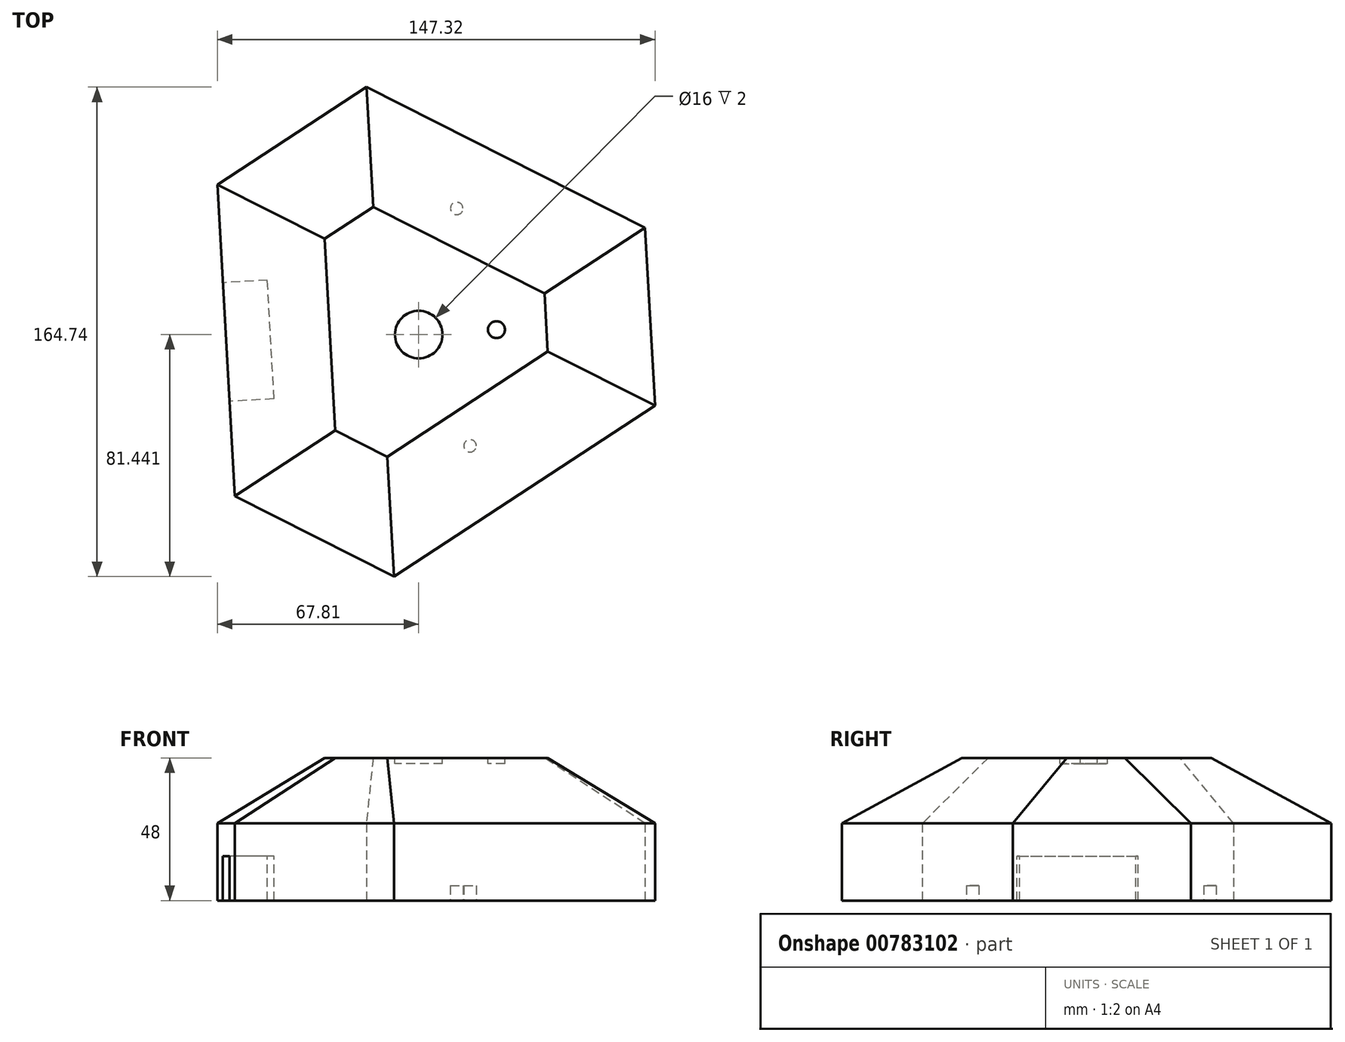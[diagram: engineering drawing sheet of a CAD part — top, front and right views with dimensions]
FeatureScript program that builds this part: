
annotation { "Feature Type Name" : "Feature", "Feature Type Description" : "" }
export const myFeature = defineFeature(function(context is Context, id is Id, definition is map)
    precondition{}
    {
        {
            var Q0;
            Q0=qCreatedBy(makeId("Top.planeOp"),FACE);
            var sketch = newSketch(context, id + "F0", { "sketchPlane" : qUnion([Q0])});
            skCircle(sketch, "E0.cCircle", {"center": v(0, 0) * mm, "radius": 64.95 * mm, "construction": true});
            skLineSegment(sketch, "E0.0", {"start": v(129.7, 7.33) * mm, "end": v(-58.5, -115.99) * mm});
            skLineSegment(sketch, "E0.1", {"start": v(-58.5, -115.99) * mm, "end": v(-71.2, 108.66) * mm});
            skLineSegment(sketch, "E0.2", {"start": v(-71.2, 108.66) * mm, "end": v(129.7, 7.33) * mm});
            skPoint(sketch, "E0.0.midPoint", {"position": v(35.6, -54.33) * mm});
            skPoint(sketch, "E1", {"position": v(-17.63, 81.64) * mm});
            skPoint(sketch, "E2", {"position": v(-67.81, 48.75) * mm});
            skPoint(sketch, "E3", {"position": v(-61.9, -55.99) * mm});
            skPoint(sketch, "E4", {"position": v(-8.31, -83.1) * mm});
            skPoint(sketch, "E5", {"position": v(79.51, -25.55) * mm});
            skPoint(sketch, "E6", {"position": v(76.13, 34.35) * mm});
            skLineSegment(sketch, "E7", {"start": v(-61.9, -55.99) * mm, "end": v(-8.31, -83.1) * mm});
            skLineSegment(sketch, "E8", {"start": v(79.51, -25.55) * mm, "end": v(76.13, 34.35) * mm});
            skLineSegment(sketch, "E9", {"start": v(-17.63, 81.64) * mm, "end": v(-67.81, 48.75) * mm});
            skSolve(sketch);
        }
        {
            var Q0;
            {var subQ3=sQuery(id+"F0.wireOp",EDGE,"E7");Q0=makeQuery(id+"F0.imprint","IMPRINT",FACE,{"disambiguationData":[TD([[makeQuery(id+"F0.imprint","IMPRINT",EDGE,{"derivedFrom":subQ3}),1.0]])]});}
            extrude(context, id + "F1", {"entities" : qUnion([Q0]), "depth" : 48 * mm, "offsetDistance" : 25 * mm});
        }
        {
            var Q0;
            Q0=makeQuery(id+"F1.opExtrude","CAP_FACE",FACE,{"disambiguationData":[OSD([sQuery(id+"F0.wireOp",EDGE,"E0.0"),sQuery(id+"F0.wireOp",EDGE,"E0.1"),sQuery(id+"F0.wireOp",EDGE,"E0.2"),sQuery(id+"F0.wireOp",EDGE,"E7"),sQuery(id+"F0.wireOp",EDGE,"E8"),sQuery(id+"F0.wireOp",EDGE,"E9")])],"isStart":false});
            chamfer(context, id + "F2", {"entities" : qUnion([Q0]), "chamferType" : ChamferType.TWO_OFFSETS, "width1" : 22 * mm, "oppositeDirection" : false, "width2" : 35 * mm, "tangentPropagation" : true});
        }
        {
            var Q0;
            Q0=makeQuery(id+"F1.opExtrude","CAP_FACE",FACE,{"disambiguationData":[OSD([sQuery(id+"F0.wireOp",EDGE,"E0.0"),sQuery(id+"F0.wireOp",EDGE,"E0.1"),sQuery(id+"F0.wireOp",EDGE,"E0.2"),sQuery(id+"F0.wireOp",EDGE,"E7"),sQuery(id+"F0.wireOp",EDGE,"E8"),sQuery(id+"F0.wireOp",EDGE,"E9")])],"isStart":false});
            var sketch = newSketch(context, id + "F3", { "sketchPlane" : qUnion([Q0])});
            skCircle(sketch, "E10", {"center": v(0, -1.66) * mm, "radius": 8 * mm});
            skPoint(sketch, "E10.centerSnap0", {"position": v(-29.9, -1.66) * mm});
            skSolve(sketch);
        }
        {
            var Q0;
            Q0 = qSketchRegion(id + "F3", true);
            extrude(context, id + "F4", {"entities" : qUnion([Q0]), "operationType" : NewBodyOperationType.REMOVE, "oppositeDirection" : true, "depth" : 2 * mm, "offsetDistance" : 25 * mm});
        }
        {
            var Q0;
            Q0=makeQuery(id+"F1.opExtrude","CAP_FACE",FACE,{"disambiguationData":[OSD([sQuery(id+"F0.wireOp",EDGE,"E0.0"),sQuery(id+"F0.wireOp",EDGE,"E0.1"),sQuery(id+"F0.wireOp",EDGE,"E0.2"),sQuery(id+"F0.wireOp",EDGE,"E7"),sQuery(id+"F0.wireOp",EDGE,"E8"),sQuery(id+"F0.wireOp",EDGE,"E9")])],"isStart":true});
            var sketch = newSketch(context, id + "F5", { "sketchPlane" : qUnion([Q0])});
            skLineSegment(sketch, "E11", {"start": v(18.77, 65.36) * mm, "end": v(11.28, -67.06) * mm, "construction": true});
            skPoint(sketch, "E12", {"position": v(15.02, -0.85) * mm});
            skCircle(sketch, "E13", {"center": v(17.28, 39.09) * mm, "radius": 2.1 * mm});
            skCircle(sketch, "E14", {"center": v(12.77, -40.79) * mm, "radius": 2.1 * mm});
            skSolve(sketch);
        }
        {
            var Q0;
            Q0 = qSketchRegion(id + "F5", true);
            extrude(context, id + "F6", {"entities" : qUnion([Q0]), "operationType" : NewBodyOperationType.REMOVE, "oppositeDirection" : true, "depth" : 5 * mm, "offsetDistance" : 25 * mm});
        }
        {
            var Q0;
            Q0=makeQuery(id+"F1.opExtrude","SWEPT_FACE",FACE,{"disambiguationData":[OSD([sQuery(id+"F0.wireOp",EDGE,"E0.1")])]});
            var sketch = newSketch(context, id + "F7", { "sketchPlane" : qUnion([Q0])});
            skLineSegment(sketch, "E15.bottom", {"start": v(20.5, 0) * mm, "end": v(-19.5, 0) * mm});
            skLineSegment(sketch, "E15.top", {"start": v(20.5, 15) * mm, "end": v(-19.5, 15) * mm});
            skLineSegment(sketch, "E15.left", {"start": v(20.5, 0) * mm, "end": v(20.5, 15) * mm});
            skLineSegment(sketch, "E15.right", {"start": v(-19.5, 0) * mm, "end": v(-19.5, 15) * mm});
            skSolve(sketch);
        }
        {
            var Q0;
            Q0 = qSketchRegion(id + "F7", true);
            extrude(context, id + "F8", {"entities" : qUnion([Q0]), "operationType" : NewBodyOperationType.REMOVE, "oppositeDirection" : true, "depth" : 15 * mm, "offsetDistance" : 25 * mm});
        }
        {
            var Q0;
            Q0=makeQuery(id+"F1.opExtrude","CAP_FACE",FACE,{"disambiguationData":[OSD([sQuery(id+"F0.wireOp",EDGE,"E0.0"),sQuery(id+"F0.wireOp",EDGE,"E0.1"),sQuery(id+"F0.wireOp",EDGE,"E0.2"),sQuery(id+"F0.wireOp",EDGE,"E7"),sQuery(id+"F0.wireOp",EDGE,"E8"),sQuery(id+"F0.wireOp",EDGE,"E9")])],"isStart":false});
            var sketch = newSketch(context, id + "F9", { "sketchPlane" : qUnion([Q0])});
            skCircle(sketch, "E16", {"center": v(26.16, 0) * mm, "radius": 2.85 * mm});
            skSolve(sketch);
        }
        {
            var Q0;
            Q0 = qSketchRegion(id + "F9", true);
            extrude(context, id + "F10", {"entities" : qUnion([Q0]), "operationType" : NewBodyOperationType.REMOVE, "oppositeDirection" : true, "depth" : 2 * mm, "offsetDistance" : 25 * mm});
        }
    });
